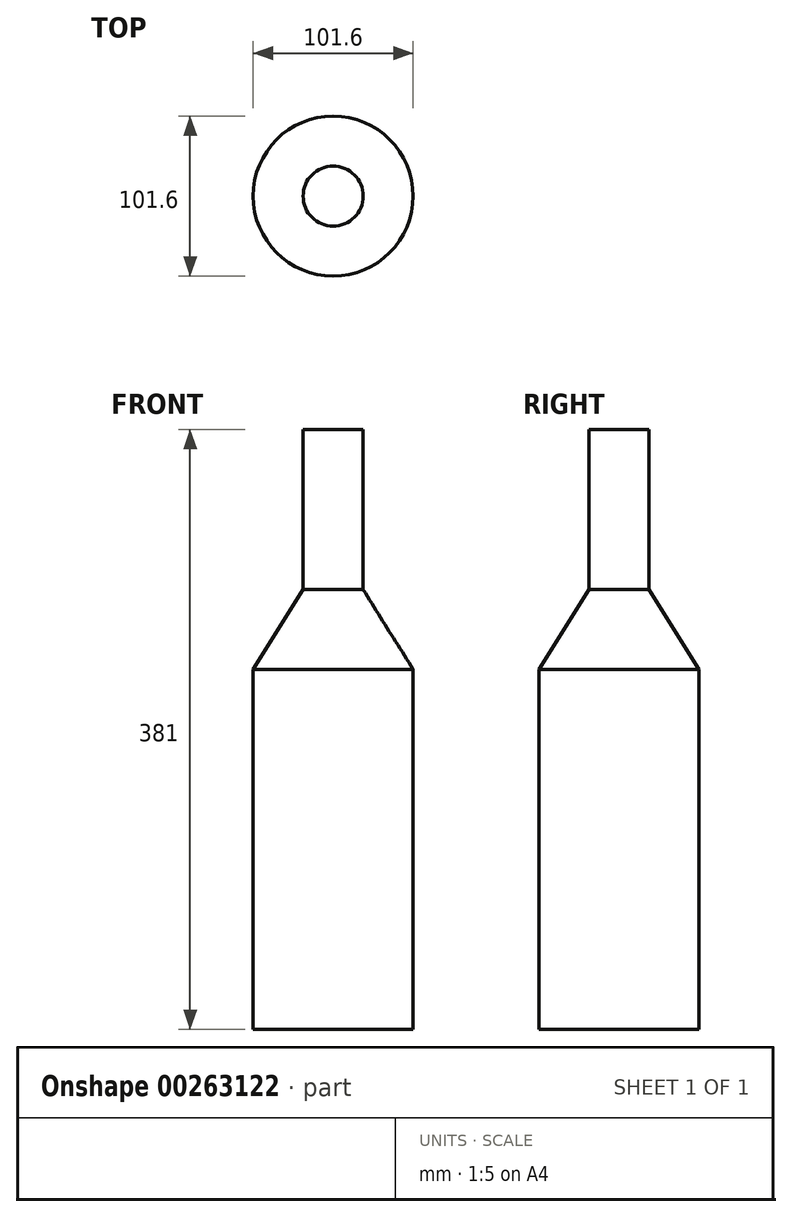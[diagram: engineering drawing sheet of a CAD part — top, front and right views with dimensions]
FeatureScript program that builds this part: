
annotation { "Feature Type Name" : "Feature", "Feature Type Description" : "" }
export const myFeature = defineFeature(function(context is Context, id is Id, definition is map)
    precondition{}
    {
        {
            var Q0;
            Q0=qCreatedBy(makeId("Front.planeOp"),FACE);
            var sketch = newSketch(context, id + "F0", { "sketchPlane" : qUnion([Q0])});
            skLineSegment(sketch, "E0", {"start": v(50.8, 0) * mm, "end": v(50.8, 228.6) * mm});
            skLineSegment(sketch, "E1", {"start": v(19.05, 381) * mm, "end": v(19.05, 279.4) * mm});
            skLineSegment(sketch, "E2", {"start": v(19.05, 279.4) * mm, "end": v(50.8, 228.6) * mm});
            skLineSegment(sketch, "E3", {"start": v(0, 381) * mm, "end": v(0, 0) * mm});
            skLineSegment(sketch, "E4", {"start": v(0, 381) * mm, "end": v(19.05, 381) * mm});
            skLineSegment(sketch, "E5", {"start": v(0, 0) * mm, "end": v(50.8, 0) * mm});
            skSolve(sketch);
        }
        {
            var Q0;
            Q0 = qSketchRegion(id + "F0", true);
            var Q1;
            Q1=sQuery(id+"F0.wireOp",EDGE,"E3");
            revolve(context, id + "F1", {"entities" : qUnion([Q0]), "axis" : qUnion([Q1]), "revolveType" : RevolveType.FULL});
        }
    });
